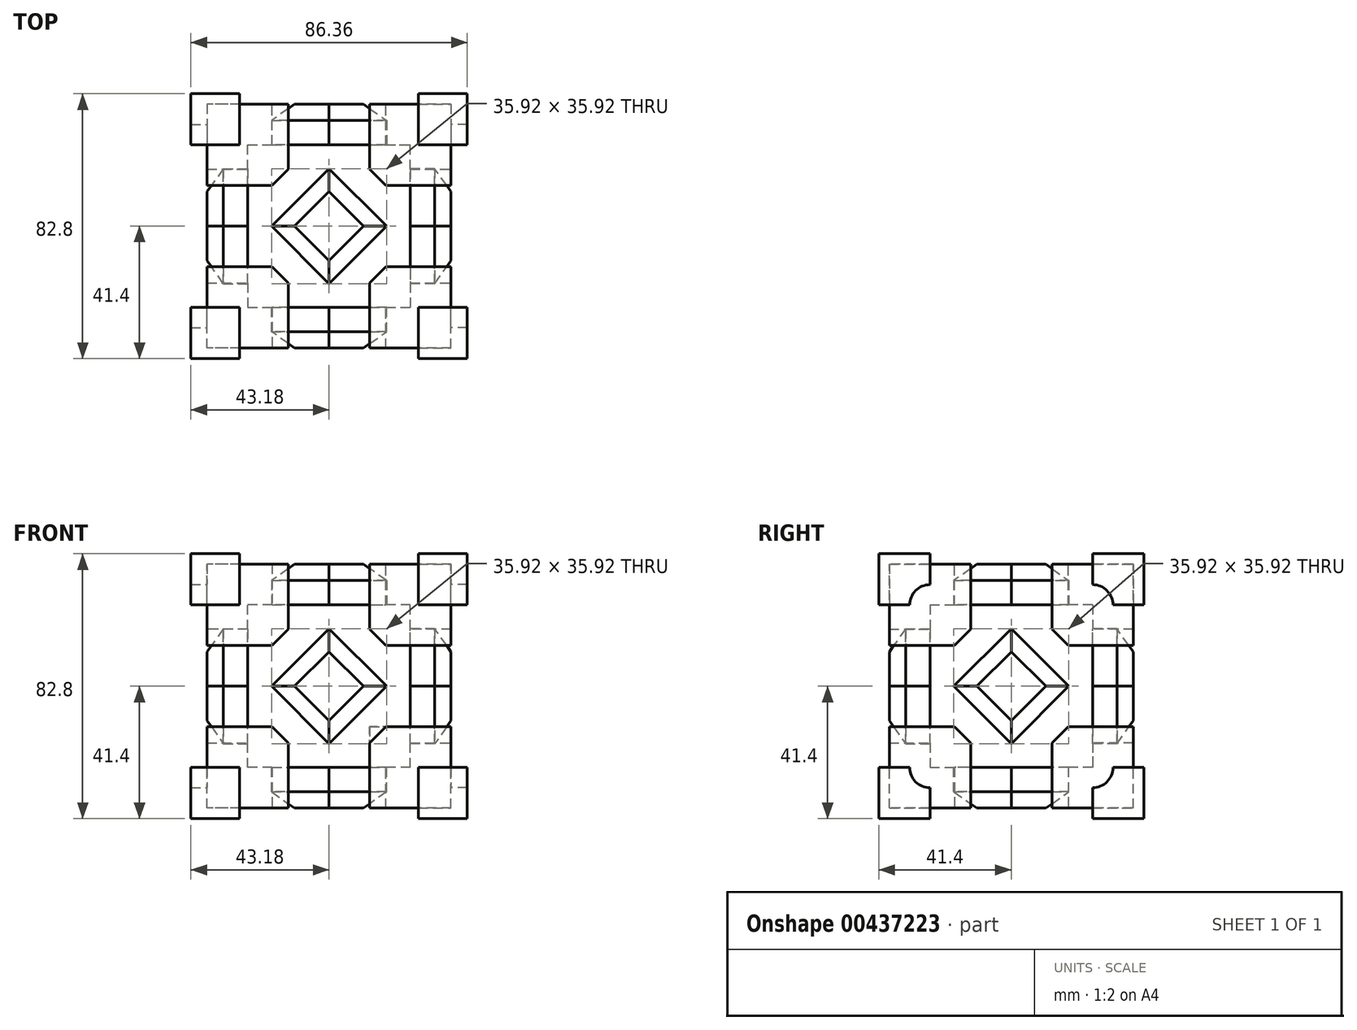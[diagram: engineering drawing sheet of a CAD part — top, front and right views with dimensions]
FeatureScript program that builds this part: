
annotation { "Feature Type Name" : "Feature", "Feature Type Description" : "" }
export const myFeature = defineFeature(function(context is Context, id is Id, definition is map)
    precondition{}
    {
        {
            var Q0;
            Q0=qCreatedBy(makeId("Front.planeOp"),FACE);
            var sketch = newSketch(context, id + "F0", { "sketchPlane" : qUnion([Q0])});
            skLineSegment(sketch, "E0.bottom", {"start": v(25.4, -25.4) * mm, "end": v(-25.4, -25.4) * mm});
            skLineSegment(sketch, "E0.top", {"start": v(25.4, 25.4) * mm, "end": v(-25.4, 25.4) * mm});
            skLineSegment(sketch, "E0.left", {"start": v(25.4, -25.4) * mm, "end": v(25.4, 25.4) * mm});
            skLineSegment(sketch, "E0.right", {"start": v(-25.4, -25.4) * mm, "end": v(-25.4, 25.4) * mm});
            skPoint(sketch, "E0.middle", {"position": v(0, 0) * mm});
            skSolve(sketch);
        }
        {
            var Q0;
            Q0 = qSketchRegion(id + "F0", true);
            extrude(context, id + "F1", {"entities" : qUnion([Q0]), "depth" : 25.4 * mm, "hasSecondDirection" : true, "secondDirectionOppositeDirection" : true, "secondDirectionDepth" : 25.4 * mm});
        }
        {
            var Q0;
            Q0=makeQuery(id+"F1.opExtrude","CAP_FACE",FACE,{"disambiguationData":[OSD([sQuery(id+"F0.wireOp",EDGE,"E0.bottom"),sQuery(id+"F0.wireOp",EDGE,"E0.top"),sQuery(id+"F0.wireOp",EDGE,"E0.left"),sQuery(id+"F0.wireOp",EDGE,"E0.right")])],"isStart":false});
            var sketch = newSketch(context, id + "F2", { "sketchPlane" : qUnion([Q0])});
            skLineSegment(sketch, "E1.bottom", {"start": v(-12.7, 12.7) * mm, "end": v(-38.1, 12.7) * mm});
            skLineSegment(sketch, "E1.top", {"start": v(-12.7, 38.1) * mm, "end": v(-38.1, 38.1) * mm});
            skLineSegment(sketch, "E1.left", {"start": v(-12.7, 12.7) * mm, "end": v(-12.7, 38.1) * mm});
            skLineSegment(sketch, "E1.right", {"start": v(-38.1, 12.7) * mm, "end": v(-38.1, 38.1) * mm});
            skPoint(sketch, "E1.middle", {"position": v(-25.4, 25.4) * mm});
            skLineSegment(sketch, "E2.bottom", {"start": v(38.1, 12.7) * mm, "end": v(12.7, 12.7) * mm});
            skLineSegment(sketch, "E2.top", {"start": v(38.1, 38.1) * mm, "end": v(12.7, 38.1) * mm});
            skLineSegment(sketch, "E2.left", {"start": v(38.1, 12.7) * mm, "end": v(38.1, 38.1) * mm});
            skLineSegment(sketch, "E2.right", {"start": v(12.7, 12.7) * mm, "end": v(12.7, 38.1) * mm});
            skPoint(sketch, "E2.middle", {"position": v(25.4, 25.4) * mm});
            skLineSegment(sketch, "E3.bottom", {"start": v(38.1, -38.1) * mm, "end": v(12.7, -38.1) * mm});
            skLineSegment(sketch, "E3.top", {"start": v(38.1, -12.7) * mm, "end": v(12.7, -12.7) * mm});
            skLineSegment(sketch, "E3.left", {"start": v(38.1, -38.1) * mm, "end": v(38.1, -12.7) * mm});
            skLineSegment(sketch, "E3.right", {"start": v(12.7, -38.1) * mm, "end": v(12.7, -12.7) * mm});
            skPoint(sketch, "E3.middle", {"position": v(25.4, -25.4) * mm});
            skLineSegment(sketch, "E4.bottom", {"start": v(-12.7, -38.1) * mm, "end": v(-38.1, -38.1) * mm});
            skLineSegment(sketch, "E4.top", {"start": v(-12.7, -12.7) * mm, "end": v(-38.1, -12.7) * mm});
            skLineSegment(sketch, "E4.left", {"start": v(-12.7, -38.1) * mm, "end": v(-12.7, -12.7) * mm});
            skLineSegment(sketch, "E4.right", {"start": v(-38.1, -38.1) * mm, "end": v(-38.1, -12.7) * mm});
            skPoint(sketch, "E4.middle", {"position": v(-25.4, -25.4) * mm});
            skCircle(sketch, "E5.cCircle", {"center": v(0, 0) * mm, "radius": 17.96 * mm, "construction": true});
            skPoint(sketch, "E5.cCircle.perimeterSnap0", {"position": v(0, 25.4) * mm});
            skLineSegment(sketch, "E5.0", {"start": v(0, 17.96) * mm, "end": v(17.96, 0) * mm});
            skPoint(sketch, "E5.0.startSnap0", {"position": v(0, 25.4) * mm});
            skLineSegment(sketch, "E5.1", {"start": v(17.96, 0) * mm, "end": v(0, -17.96) * mm});
            skLineSegment(sketch, "E5.2", {"start": v(0, -17.96) * mm, "end": v(-17.96, 0) * mm});
            skLineSegment(sketch, "E5.3", {"start": v(-17.96, 0) * mm, "end": v(0, 17.96) * mm});
            skSolve(sketch);
        }
        {
            var Q0;
            Q0 = qSketchRegion(id + "F2", true);
            extrude(context, id + "F3", {"entities" : qUnion([Q0]), "operationType" : NewBodyOperationType.ADD, "depth" : 12.7 * mm, "hasSecondDirection" : true, "secondDirectionOppositeDirection" : true, "secondDirectionDepth" : 12.7 * mm});
        }
        {
            var Q0;
            Q0=makeQuery(id+"F1.opExtrude","SWEPT_BODY",BODY,{"disambiguationData":[OSD([sQuery(id+"F0.wireOp",EDGE,"E0.bottom"),sQuery(id+"F0.wireOp",EDGE,"E0.top"),sQuery(id+"F0.wireOp",EDGE,"E0.left"),sQuery(id+"F0.wireOp",EDGE,"E0.right")])]});
            var Q1;
            Q1=qCreatedBy(makeId("Front.planeOp"),FACE);
            mirror(context, id + "F4", {"operationType" : NewBodyOperationType.ADD, "entities" : qUnion([Q0]), "mirrorPlane" : qUnion([Q1])});
        }
        {
            var Q0;
            Q0=makeQuery(id+"F1.opExtrude","SWEPT_FACE",FACE,{"disambiguationData":[OSD([sQuery(id+"F0.wireOp",EDGE,"E0.bottom")])]});
            var sketch = newSketch(context, id + "F5", { "sketchPlane" : qUnion([Q0])});
            skCircle(sketch, "E6.cCircle", {"center": v(0, 0) * mm, "radius": 17.96 * mm, "construction": true});
            skLineSegment(sketch, "E6.0", {"start": v(0, 17.96) * mm, "end": v(17.96, 0) * mm});
            skLineSegment(sketch, "E6.1", {"start": v(17.96, 0) * mm, "end": v(0, -17.96) * mm});
            skLineSegment(sketch, "E6.2", {"start": v(0, -17.96) * mm, "end": v(-17.96, 0) * mm});
            skLineSegment(sketch, "E6.3", {"start": v(-17.96, 0) * mm, "end": v(0, 17.96) * mm});
            skSolve(sketch);
        }
        {
            var Q0;
            Q0 = qSketchRegion(id + "F5", true);
            extrude(context, id + "F6", {"entities" : qUnion([Q0]), "operationType" : NewBodyOperationType.ADD, "depth" : 12.7 * mm, "hasSecondDirection" : true, "secondDirectionOppositeDirection" : true, "secondDirectionDepth" : 12.7 * mm});
        }
        {
            var Q0;
            Q0=makeQuery(id+"F1.opExtrude","SWEPT_BODY",BODY,{"disambiguationData":[OSD([sQuery(id+"F0.wireOp",EDGE,"E0.bottom"),sQuery(id+"F0.wireOp",EDGE,"E0.top"),sQuery(id+"F0.wireOp",EDGE,"E0.left"),sQuery(id+"F0.wireOp",EDGE,"E0.right")])]});
            var Q1;
            Q1=qCreatedBy(makeId("Top.planeOp"),FACE);
            mirror(context, id + "F7", {"operationType" : NewBodyOperationType.ADD, "entities" : qUnion([Q0]), "mirrorPlane" : qUnion([Q1])});
        }
        {
            var Q0;
            Q0=makeQuery(id+"F1.opExtrude","SWEPT_FACE",FACE,{"disambiguationData":[OSD([sQuery(id+"F0.wireOp",EDGE,"E0.right")])]});
            var sketch = newSketch(context, id + "F8", { "sketchPlane" : qUnion([Q0])});
            skCircle(sketch, "E7.cCircle", {"center": v(0, 0) * mm, "radius": 17.96 * mm, "construction": true});
            skLineSegment(sketch, "E7.0", {"start": v(0, 17.96) * mm, "end": v(17.96, 0) * mm});
            skLineSegment(sketch, "E7.1", {"start": v(17.96, 0) * mm, "end": v(0, -17.96) * mm});
            skLineSegment(sketch, "E7.2", {"start": v(0, -17.96) * mm, "end": v(-17.96, 0) * mm});
            skLineSegment(sketch, "E7.3", {"start": v(-17.96, 0) * mm, "end": v(0, 17.96) * mm});
            skSolve(sketch);
        }
        {
            var Q0;
            Q0 = qSketchRegion(id + "F8", true);
            extrude(context, id + "F9", {"entities" : qUnion([Q0]), "operationType" : NewBodyOperationType.ADD, "depth" : 12.7 * mm, "hasSecondDirection" : true, "secondDirectionOppositeDirection" : true, "secondDirectionDepth" : 12.7 * mm});
        }
        {
            var Q0;
            Q0=makeQuery(id+"F4.opPattern","COPY",FACE,{"derivedFrom":makeQuery(id+"F3.opExtrude","SWEPT_FACE",FACE,{"disambiguationData":[OSD([sQuery(id+"F2.wireOp",EDGE,"E4.right")])]}),"instanceName":"1"});
            var sketch = newSketch(context, id + "F10", { "sketchPlane" : qUnion([Q0])});
            skLineSegment(sketch, "E8", {"start": v(-38.1, -25.4) * mm, "end": v(-31.75, -25.4) * mm});
            skLineSegment(sketch, "E9", {"start": v(-25.4, -31.75) * mm, "end": v(-25.4, -38.1) * mm});
            skLineSegment(sketch, "E10", {"start": v(-25.4, -38.1) * mm, "end": v(-25.4, -41.4) * mm});
            skLineSegment(sketch, "E11", {"start": v(-38.1, -25.4) * mm, "end": v(-41.4, -25.4) * mm});
            skLineSegment(sketch, "E12", {"start": v(-41.4, -25.4) * mm, "end": v(-41.4, -38.1) * mm});
            skLineSegment(sketch, "E13", {"start": v(-25.4, -41.4) * mm, "end": v(-38.1, -41.4) * mm});
            skLineSegment(sketch, "E14", {"start": v(-38.1, -41.4) * mm, "end": v(-41.4, -41.4) * mm});
            skLineSegment(sketch, "E15", {"start": v(-41.4, -41.4) * mm, "end": v(-41.4, -38.1) * mm});
            skArc(sketch, "E16", {"start": v(-31.75, -25.4) * mm, "mid": v(-29.9, -29.9) * mm, "end": v(-25.4, -31.75) * mm});
            skSolve(sketch);
        }
        {
            var Q0;
            {var subQ5=sQuery(id+"F10.wireOp",EDGE,"E10");Q0=makeQuery(id+"F10.imprint","IMPRINT",FACE,{"disambiguationData":[TD([[makeQuery(id+"F10.imprint","IMPRINT",EDGE,{"derivedFrom":subQ5}),-1.0]])]});}
            var Q1;
            {var subQ5=sQuery(id+"F10.wireOp",EDGE,"E8");Q1=makeQuery(id+"F10.imprint","IMPRINT",FACE,{"disambiguationData":[TD([[makeQuery(id+"F10.imprint","IMPRINT",EDGE,{"derivedFrom":subQ5}),-1.0]])]});}
            extrude(context, id + "F11", {"entities" : qUnion([Q0, Q1]), "operationType" : NewBodyOperationType.ADD, "depth" : 5.08 * mm, "hasSecondDirection" : true, "secondDirectionOppositeDirection" : true, "secondDirectionDepth" : 10.16 * mm});
        }
        {
            var Q0;
            Q0=makeQuery(id+"F1.opExtrude","SWEPT_BODY",BODY,{"disambiguationData":[OSD([sQuery(id+"F0.wireOp",EDGE,"E0.bottom"),sQuery(id+"F0.wireOp",EDGE,"E0.top"),sQuery(id+"F0.wireOp",EDGE,"E0.left"),sQuery(id+"F0.wireOp",EDGE,"E0.right")])]});
            var Q1;
            Q1=qCreatedBy(makeId("Right.planeOp"),FACE);
            mirror(context, id + "F12", {"operationType" : NewBodyOperationType.ADD, "entities" : qUnion([Q0]), "mirrorPlane" : qUnion([Q1])});
        }
        {
            var Q0;
            Q0=makeQuery(id+"F1.opExtrude","SWEPT_BODY",BODY,{"disambiguationData":[OSD([sQuery(id+"F0.wireOp",EDGE,"E0.bottom"),sQuery(id+"F0.wireOp",EDGE,"E0.top"),sQuery(id+"F0.wireOp",EDGE,"E0.left"),sQuery(id+"F0.wireOp",EDGE,"E0.right")])]});
            var Q1;
            Q1=qCreatedBy(makeId("Top.planeOp"),FACE);
            mirror(context, id + "F13", {"operationType" : NewBodyOperationType.ADD, "entities" : qUnion([Q0]), "mirrorPlane" : qUnion([Q1])});
        }
        {
            var Q0;
            Q0=makeQuery(id+"F1.opExtrude","SWEPT_BODY",BODY,{"disambiguationData":[OSD([sQuery(id+"F0.wireOp",EDGE,"E0.bottom"),sQuery(id+"F0.wireOp",EDGE,"E0.top"),sQuery(id+"F0.wireOp",EDGE,"E0.left"),sQuery(id+"F0.wireOp",EDGE,"E0.right")])]});
            var Q1;
            Q1=qCreatedBy(makeId("Front.planeOp"),FACE);
            mirror(context, id + "F14", {"operationType" : NewBodyOperationType.ADD, "entities" : qUnion([Q0]), "mirrorPlane" : qUnion([Q1])});
        }
        {
            var Q0;
            Q0=makeQuery(id+"F1.opExtrude","SWEPT_BODY",BODY,{"disambiguationData":[OSD([sQuery(id+"F0.wireOp",EDGE,"E0.bottom"),sQuery(id+"F0.wireOp",EDGE,"E0.top"),sQuery(id+"F0.wireOp",EDGE,"E0.left"),sQuery(id+"F0.wireOp",EDGE,"E0.right")])]});
            var Q1;
            Q1=qCreatedBy(makeId("Right.planeOp"),FACE);
            mirror(context, id + "F15", {"operationType" : NewBodyOperationType.INTERSECT, "entities" : qUnion([Q0]), "mirrorPlane" : qUnion([Q1])});
        }
        {
            var Q0;
            Q0=makeQuery(id+"F4.opPattern","COPY",EDGE,{"derivedFrom":makeQuery(id+"F3.opExtrude","CAP_EDGE",EDGE,{"disambiguationData":[OSD([sQuery(id+"F2.wireOp",EDGE,"E3.right")])],"isStart":true}),"instanceName":"1"});
            var Q1;
            Q1=makeQuery(id+"F3.opExtrude","CAP_EDGE",EDGE,{"disambiguationData":[OSD([sQuery(id+"F2.wireOp",EDGE,"E3.right")])],"isStart":true});
            var Q2;
            Q2=makeQuery(id+"F3.opExtrude","CAP_EDGE",EDGE,{"disambiguationData":[OSD([sQuery(id+"F2.wireOp",EDGE,"E4.left")])],"isStart":true});
            var Q3;
            Q3=makeQuery(id+"F4.opPattern","COPY",EDGE,{"derivedFrom":makeQuery(id+"F3.opExtrude","CAP_EDGE",EDGE,{"disambiguationData":[OSD([sQuery(id+"F2.wireOp",EDGE,"E4.left")])],"isStart":true}),"instanceName":"1"});
            var Q4;
            Q4=makeQuery(id+"F4.opPattern","COPY",EDGE,{"derivedFrom":makeQuery(id+"F3.opExtrude","SWEPT_EDGE",EDGE,{"disambiguationData":[OSD([sQuery(id+"F2.wireOp",EDGE,"E4.top"),sQuery(id+"F2.wireOp",EDGE,"E4.left")])]}),"instanceName":"1"});
            var Q5;
            Q5=makeQuery(id+"F4.opPattern","COPY",EDGE,{"derivedFrom":makeQuery(id+"F3.opExtrude","SWEPT_EDGE",EDGE,{"disambiguationData":[OSD([sQuery(id+"F2.wireOp",EDGE,"E2.bottom"),sQuery(id+"F2.wireOp",EDGE,"E2.right")])]}),"instanceName":"1"});
            var Q6;
            Q6=makeQuery(id+"F4.opPattern","COPY",EDGE,{"derivedFrom":makeQuery(id+"F3.opExtrude","SWEPT_EDGE",EDGE,{"disambiguationData":[OSD([sQuery(id+"F2.wireOp",EDGE,"E1.bottom"),sQuery(id+"F2.wireOp",EDGE,"E1.left")])]}),"instanceName":"1"});
            var Q7;
            Q7=makeQuery(id+"F4.opPattern","COPY",EDGE,{"derivedFrom":makeQuery(id+"F3.opExtrude","CAP_EDGE",EDGE,{"disambiguationData":[OSD([sQuery(id+"F2.wireOp",EDGE,"E2.bottom")])],"isStart":true}),"instanceName":"1"});
            var Q8;
            Q8=makeQuery(id+"F3.opExtrude","CAP_EDGE",EDGE,{"disambiguationData":[OSD([sQuery(id+"F2.wireOp",EDGE,"E2.bottom")])],"isStart":true});
            var Q9;
            Q9=makeQuery(id+"F3.opExtrude","CAP_EDGE",EDGE,{"disambiguationData":[OSD([sQuery(id+"F2.wireOp",EDGE,"E3.top")])],"isStart":true});
            var Q10;
            Q10=makeQuery(id+"F4.opPattern","COPY",EDGE,{"derivedFrom":makeQuery(id+"F3.opExtrude","CAP_EDGE",EDGE,{"disambiguationData":[OSD([sQuery(id+"F2.wireOp",EDGE,"E3.top")])],"isStart":true}),"instanceName":"1"});
            var Q11;
            Q11=makeQuery(id+"F3.opExtrude","CAP_EDGE",EDGE,{"disambiguationData":[OSD([sQuery(id+"F2.wireOp",EDGE,"E1.left")])],"isStart":true});
            var Q12;
            Q12=makeQuery(id+"F4.opPattern","COPY",EDGE,{"derivedFrom":makeQuery(id+"F3.opExtrude","CAP_EDGE",EDGE,{"disambiguationData":[OSD([sQuery(id+"F2.wireOp",EDGE,"E1.left")])],"isStart":true}),"instanceName":"1"});
            var Q13;
            Q13=makeQuery(id+"F3.opExtrude","SWEPT_EDGE",EDGE,{"disambiguationData":[OSD([sQuery(id+"F2.wireOp",EDGE,"E2.bottom"),sQuery(id+"F2.wireOp",EDGE,"E2.right")])]});
            var Q14;
            Q14=makeQuery(id+"F3.opExtrude","SWEPT_EDGE",EDGE,{"disambiguationData":[OSD([sQuery(id+"F2.wireOp",EDGE,"E4.top"),sQuery(id+"F2.wireOp",EDGE,"E4.left")])]});
            var Q15;
            Q15=makeQuery(id+"F3.opExtrude","SWEPT_EDGE",EDGE,{"disambiguationData":[OSD([sQuery(id+"F2.wireOp",EDGE,"E3.top"),sQuery(id+"F2.wireOp",EDGE,"E3.right")])]});
            var Q16;
            Q16=makeQuery(id+"F4.opPattern","COPY",EDGE,{"derivedFrom":makeQuery(id+"F3.opExtrude","CAP_EDGE",EDGE,{"disambiguationData":[OSD([sQuery(id+"F2.wireOp",EDGE,"E2.right")])],"isStart":true}),"instanceName":"1"});
            var Q17;
            Q17=makeQuery(id+"F3.opExtrude","CAP_EDGE",EDGE,{"disambiguationData":[OSD([sQuery(id+"F2.wireOp",EDGE,"E2.right")])],"isStart":true});
            var Q18;
            Q18=makeQuery(id+"F4.opPattern","COPY",EDGE,{"derivedFrom":makeQuery(id+"F3.opExtrude","CAP_EDGE",EDGE,{"disambiguationData":[OSD([sQuery(id+"F2.wireOp",EDGE,"E4.top")])],"isStart":true}),"instanceName":"1"});
            var Q19;
            Q19=makeQuery(id+"F4.opPattern","COPY",EDGE,{"derivedFrom":makeQuery(id+"F3.opExtrude","CAP_EDGE",EDGE,{"disambiguationData":[OSD([sQuery(id+"F2.wireOp",EDGE,"E1.bottom")])],"isStart":true}),"instanceName":"1"});
            var Q20;
            Q20=makeQuery(id+"F3.opExtrude","CAP_EDGE",EDGE,{"disambiguationData":[OSD([sQuery(id+"F2.wireOp",EDGE,"E4.top")])],"isStart":true});
            var Q21;
            Q21=makeQuery(id+"F3.opExtrude","CAP_EDGE",EDGE,{"disambiguationData":[OSD([sQuery(id+"F2.wireOp",EDGE,"E1.bottom")])],"isStart":true});
            var Q22;
            Q22=makeQuery(id+"F3.opExtrude","SWEPT_EDGE",EDGE,{"disambiguationData":[OSD([sQuery(id+"F2.wireOp",EDGE,"E1.bottom"),sQuery(id+"F2.wireOp",EDGE,"E1.left")])]});
            chamfer(context, id + "F16", {"entities" : qUnion([Q0, Q1, Q2, Q3, Q4, Q5, Q6, Q7, Q8, Q9, Q10, Q11, Q12, Q13, Q14, Q15, Q16, Q17, Q18, Q19, Q20, Q21, Q22]), "width" : 5.08 * mm, "tangentPropagation" : true});
        }
        {
            var Q0;
            Q0=makeQuery(id+"F9.opExtrude","CAP_FACE",FACE,{"disambiguationData":[OSD([sQuery(id+"F8.wireOp",EDGE,"E7.0"),sQuery(id+"F8.wireOp",EDGE,"E7.1"),sQuery(id+"F8.wireOp",EDGE,"E7.2"),sQuery(id+"F8.wireOp",EDGE,"E7.3")])],"isStart":false});
            var Q1;
            Q1=makeQuery(id+"F6.opExtrude","CAP_FACE",FACE,{"disambiguationData":[OSD([sQuery(id+"F5.wireOp",EDGE,"E6.0"),sQuery(id+"F5.wireOp",EDGE,"E6.1"),sQuery(id+"F5.wireOp",EDGE,"E6.2"),sQuery(id+"F5.wireOp",EDGE,"E6.3")])],"isStart":false});
            var Q2;
            Q2=makeQuery(id+"F4.opPattern","COPY",FACE,{"derivedFrom":makeQuery(id+"F3.opExtrude","CAP_FACE",FACE,{"disambiguationData":[OSD([sQuery(id+"F2.wireOp",EDGE,"E5.0"),sQuery(id+"F2.wireOp",EDGE,"E5.1"),sQuery(id+"F2.wireOp",EDGE,"E5.2"),sQuery(id+"F2.wireOp",EDGE,"E5.3")])],"isStart":false}),"instanceName":"1"});
            var Q3;
            Q3=makeQuery(id+"F7.opPattern","COPY",FACE,{"derivedFrom":makeQuery(id+"F6.opExtrude","CAP_FACE",FACE,{"disambiguationData":[OSD([sQuery(id+"F5.wireOp",EDGE,"E6.0"),sQuery(id+"F5.wireOp",EDGE,"E6.1"),sQuery(id+"F5.wireOp",EDGE,"E6.2"),sQuery(id+"F5.wireOp",EDGE,"E6.3")])],"isStart":false}),"instanceName":"1"});
            var Q4;
            Q4=makeQuery(id+"F12.opPattern","COPY",FACE,{"derivedFrom":makeQuery(id+"F9.opExtrude","CAP_FACE",FACE,{"disambiguationData":[OSD([sQuery(id+"F8.wireOp",EDGE,"E7.0"),sQuery(id+"F8.wireOp",EDGE,"E7.1"),sQuery(id+"F8.wireOp",EDGE,"E7.2"),sQuery(id+"F8.wireOp",EDGE,"E7.3")])],"isStart":false}),"instanceName":"1"});
            var Q5;
            Q5=makeQuery(id+"F3.opExtrude","CAP_FACE",FACE,{"disambiguationData":[OSD([sQuery(id+"F2.wireOp",EDGE,"E5.0"),sQuery(id+"F2.wireOp",EDGE,"E5.1"),sQuery(id+"F2.wireOp",EDGE,"E5.2"),sQuery(id+"F2.wireOp",EDGE,"E5.3")])],"isStart":false});
            chamfer(context, id + "F17", {"entities" : qUnion([Q0, Q1, Q2, Q3, Q4, Q5]), "width" : 5.08 * mm, "tangentPropagation" : true});
        }
    });
